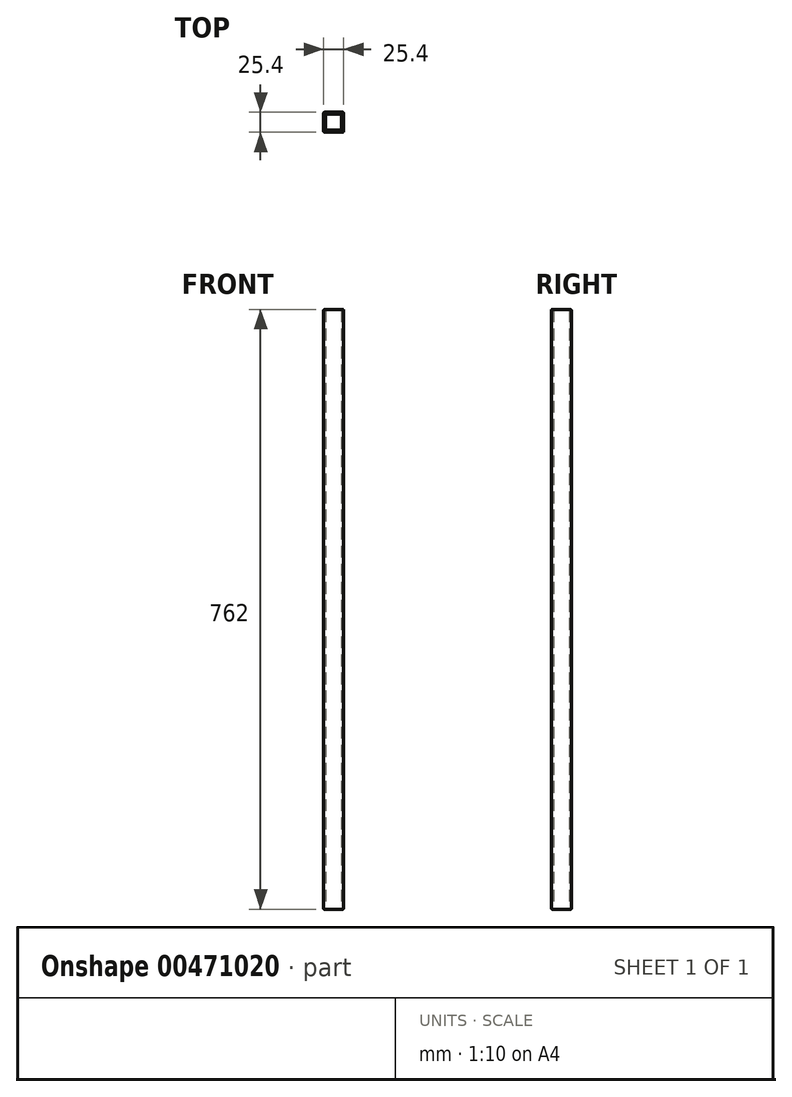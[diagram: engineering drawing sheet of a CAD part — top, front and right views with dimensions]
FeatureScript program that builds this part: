
annotation { "Feature Type Name" : "Feature", "Feature Type Description" : "" }
export const myFeature = defineFeature(function(context is Context, id is Id, definition is map)
    precondition{}
    {
        {
            var Q0;
            Q0=qCreatedBy(makeId("Top.planeOp"),FACE);
            var sketch = newSketch(context, id + "F0", { "sketchPlane" : qUnion([Q0])});
            skLineSegment(sketch, "E0.bottom", {"start": v(-12.7, -12.7) * mm, "end": v(12.7, -12.7) * mm});
            skLineSegment(sketch, "E0.top", {"start": v(-12.7, 12.7) * mm, "end": v(12.7, 12.7) * mm});
            skLineSegment(sketch, "E0.left", {"start": v(-12.7, -12.7) * mm, "end": v(-12.7, 12.7) * mm});
            skLineSegment(sketch, "E0.right", {"start": v(12.7, -12.7) * mm, "end": v(12.7, 12.7) * mm});
            skPoint(sketch, "E0.middle", {"position": v(0, 0) * mm});
            skLineSegment(sketch, "E1.bottom", {"start": v(-10.16, -10.16) * mm, "end": v(10.16, -10.16) * mm});
            skLineSegment(sketch, "E1.top", {"start": v(-10.16, 10.16) * mm, "end": v(10.16, 10.16) * mm});
            skLineSegment(sketch, "E1.left", {"start": v(-10.16, -10.16) * mm, "end": v(-10.16, 10.16) * mm});
            skLineSegment(sketch, "E1.right", {"start": v(10.16, -10.16) * mm, "end": v(10.16, 10.16) * mm});
            skSolve(sketch);
        }
        {
            var Q0;
            Q0=makeQuery(id+"F0.imprint","IMPRINT",FACE,{"disambiguationData":[TD([[makeQuery(id+"F0.imprint","IMPRINT",EDGE,{"derivedFrom":sQuery(id+"F0.wireOp",EDGE,"E0.bottom")}),1.0]])]});
            extrude(context, id + "F1", {"entities" : qUnion([Q0]), "endBound" : BoundingType.SYMMETRIC, "depth" : 762 * mm});
        }
        {
            var Q0;
            Q0=makeQuery(id+"F1.opExtrude","SWEPT_FACE",FACE,{"disambiguationData":[OSD([sQuery(id+"F0.wireOp",EDGE,"E1.bottom")])]});
            var Q1;
            Q1=makeQuery(id+"F1.opExtrude","SWEPT_FACE",FACE,{"disambiguationData":[OSD([sQuery(id+"F0.wireOp",EDGE,"E1.right")])]});
            var Q2;
            Q2=makeQuery(id+"F1.opExtrude","SWEPT_FACE",FACE,{"disambiguationData":[OSD([sQuery(id+"F0.wireOp",EDGE,"E1.left")])]});
            var Q3;
            Q3=makeQuery(id+"F1.opExtrude","SWEPT_FACE",FACE,{"disambiguationData":[OSD([sQuery(id+"F0.wireOp",EDGE,"E1.top")])]});
            var Q4;
            Q4=makeQuery(id+"F1.opExtrude","SWEPT_FACE",FACE,{"disambiguationData":[OSD([sQuery(id+"F0.wireOp",EDGE,"E0.right")])]});
            fillet(context, id + "F2", {"entities" : qUnion([Q0, Q1, Q2, Q3, Q4]), "radius" : 1.27 * mm, "tangentPropagation" : true, "allowEdgeOverflow" : false});
        }
        {
            var Q0;
            Q0=makeQuery(id+"F1.opExtrude","SWEPT_FACE",FACE,{"disambiguationData":[OSD([sQuery(id+"F0.wireOp",EDGE,"E0.bottom")])]});
            var Q1;
            Q1=makeQuery(id+"F1.opExtrude","SWEPT_FACE",FACE,{"disambiguationData":[OSD([sQuery(id+"F0.wireOp",EDGE,"E0.right")])]});
            fillet(context, id + "F3", {"entities" : qUnion([Q0, Q1]), "radius" : 1.27 * mm, "tangentPropagation" : true, "allowEdgeOverflow" : false});
        }
        {
            var Q0;
            Q0=makeQuery(id+"F1.opExtrude","SWEPT_FACE",FACE,{"disambiguationData":[OSD([sQuery(id+"F0.wireOp",EDGE,"E0.top")])]});
            var Q1;
            Q1=makeQuery(id+"F1.opExtrude","SWEPT_FACE",FACE,{"disambiguationData":[OSD([sQuery(id+"F0.wireOp",EDGE,"E0.left")])]});
            fillet(context, id + "F4", {"entities" : qUnion([Q0, Q1]), "radius" : 1.27 * mm, "tangentPropagation" : true, "allowEdgeOverflow" : false});
        }
    });
